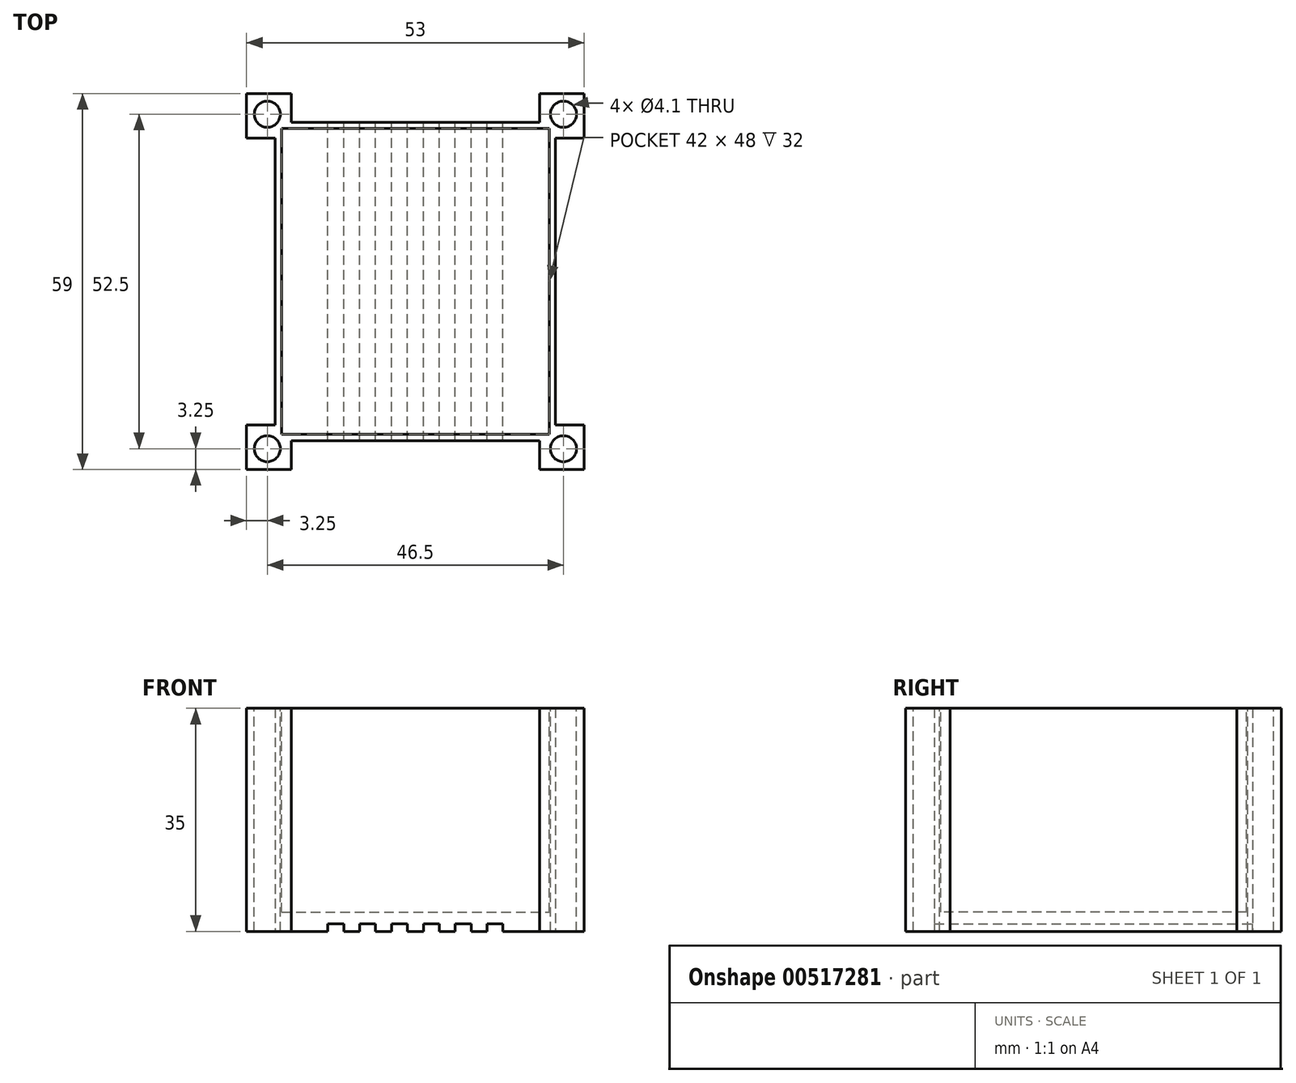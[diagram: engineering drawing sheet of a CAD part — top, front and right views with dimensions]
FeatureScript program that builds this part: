
annotation { "Feature Type Name" : "Feature", "Feature Type Description" : "" }
export const myFeature = defineFeature(function(context is Context, id is Id, definition is map)
    precondition{}
    {
        {
            var Q0;
            Q0=qCreatedBy(makeId("Top.planeOp"),FACE);
            var sketch = newSketch(context, id + "F0", { "sketchPlane" : qUnion([Q0])});
            skLineSegment(sketch, "E0.bottom", {"start": v(-22, 25) * mm, "end": v(22, 25) * mm});
            skLineSegment(sketch, "E0.top", {"start": v(-22, -25) * mm, "end": v(22, -25) * mm});
            skLineSegment(sketch, "E0.left", {"start": v(-22, 25) * mm, "end": v(-22, -25) * mm});
            skLineSegment(sketch, "E0.right", {"start": v(22, 25) * mm, "end": v(22, -25) * mm});
            skLineSegment(sketch, "E1.bottom", {"start": v(-26.5, 29.5) * mm, "end": v(-19.5, 29.5) * mm});
            skLineSegment(sketch, "E1.top", {"start": v(-26.5, 22.5) * mm, "end": v(-19.5, 22.5) * mm});
            skLineSegment(sketch, "E1.left", {"start": v(-26.5, 29.5) * mm, "end": v(-26.5, 22.5) * mm});
            skLineSegment(sketch, "E1.right", {"start": v(-19.5, 29.5) * mm, "end": v(-19.5, 22.5) * mm});
            skLineSegment(sketch, "E2.MirrorCS", {"start": v(19.5, 29.5) * mm, "end": v(19.5, 22.5) * mm});
            skLineSegment(sketch, "E3.MirrorCS", {"start": v(26.5, 22.5) * mm, "end": v(19.5, 22.5) * mm});
            skLineSegment(sketch, "E4.MirrorCS", {"start": v(26.5, 29.5) * mm, "end": v(19.5, 29.5) * mm});
            skLineSegment(sketch, "E5.MirrorCS", {"start": v(26.5, 29.5) * mm, "end": v(26.5, 22.5) * mm});
            skLineSegment(sketch, "E6.MirrorCS", {"start": v(26.5, -29.5) * mm, "end": v(26.5, -22.5) * mm});
            skLineSegment(sketch, "E7.MirrorCS", {"start": v(26.5, -29.5) * mm, "end": v(19.5, -29.5) * mm});
            skLineSegment(sketch, "E8.MirrorCS", {"start": v(26.5, -22.5) * mm, "end": v(19.5, -22.5) * mm});
            skLineSegment(sketch, "E9.MirrorCS", {"start": v(19.5, -29.5) * mm, "end": v(19.5, -22.5) * mm});
            skLineSegment(sketch, "E10.MirrorCS", {"start": v(-19.5, -29.5) * mm, "end": v(-19.5, -22.5) * mm});
            skLineSegment(sketch, "E11.MirrorCS", {"start": v(-26.5, -29.5) * mm, "end": v(-26.5, -22.5) * mm});
            skLineSegment(sketch, "E12.MirrorCS", {"start": v(-26.5, -29.5) * mm, "end": v(-19.5, -29.5) * mm});
            skLineSegment(sketch, "E13.MirrorCS", {"start": v(-26.5, -22.5) * mm, "end": v(-19.5, -22.5) * mm});
            skSolve(sketch);
        }
        {
            var Q0;
            Q0 = qSketchRegion(id + "F0", true);
            extrude(context, id + "F1", {"entities" : qUnion([Q0]), "depth" : 35 * mm, "offsetDistance" : 25 * mm});
        }
        {
            var Q0;
            Q0=makeQuery(id+"F1.opExtrude","CAP_FACE",FACE,{"disambiguationData":[OSD([sQuery(id+"F0.wireOp",EDGE,"E0.bottom"),sQuery(id+"F0.wireOp",EDGE,"E0.top"),sQuery(id+"F0.wireOp",EDGE,"E0.left"),sQuery(id+"F0.wireOp",EDGE,"E0.right"),sQuery(id+"F0.wireOp",EDGE,"E1.bottom"),sQuery(id+"F0.wireOp",EDGE,"E1.top"),sQuery(id+"F0.wireOp",EDGE,"E1.left"),sQuery(id+"F0.wireOp",EDGE,"E1.right"),sQuery(id+"F0.wireOp",EDGE,"E2.MirrorCS"),sQuery(id+"F0.wireOp",EDGE,"E3.MirrorCS"),sQuery(id+"F0.wireOp",EDGE,"E4.MirrorCS"),sQuery(id+"F0.wireOp",EDGE,"E5.MirrorCS"),sQuery(id+"F0.wireOp",EDGE,"E6.MirrorCS"),sQuery(id+"F0.wireOp",EDGE,"E7.MirrorCS"),sQuery(id+"F0.wireOp",EDGE,"E8.MirrorCS"),sQuery(id+"F0.wireOp",EDGE,"E9.MirrorCS"),sQuery(id+"F0.wireOp",EDGE,"E10.MirrorCS"),sQuery(id+"F0.wireOp",EDGE,"E11.MirrorCS"),sQuery(id+"F0.wireOp",EDGE,"E12.MirrorCS"),sQuery(id+"F0.wireOp",EDGE,"E13.MirrorCS")])],"isStart":false});
            var sketch = newSketch(context, id + "F2", { "sketchPlane" : qUnion([Q0])});
            skCircle(sketch, "E14", {"center": v(-23.25, 26.25) * mm, "radius": 2.05 * mm});
            skCircle(sketch, "E15.MirrorC", {"center": v(23.25, 26.25) * mm, "radius": 2.05 * mm});
            skCircle(sketch, "E16.MirrorC", {"center": v(-23.25, -26.25) * mm, "radius": 2.05 * mm});
            skCircle(sketch, "E17.MirrorC", {"center": v(23.25, -26.25) * mm, "radius": 2.05 * mm});
            skSolve(sketch);
        }
        {
            var Q0;
            Q0 = qSketchRegion(id + "F2", true);
            extrude(context, id + "F3", {"entities" : qUnion([Q0]), "operationType" : NewBodyOperationType.REMOVE, "endBound" : BoundingType.UP_TO_NEXT, "oppositeDirection" : true, "depth" : 25 * mm, "offsetDistance" : 25 * mm});
        }
        {
            var Q0;
            Q0=makeQuery(id+"F1.opExtrude","CAP_FACE",FACE,{"disambiguationData":[OSD([sQuery(id+"F0.wireOp",EDGE,"E0.bottom"),sQuery(id+"F0.wireOp",EDGE,"E0.top"),sQuery(id+"F0.wireOp",EDGE,"E0.left"),sQuery(id+"F0.wireOp",EDGE,"E0.right"),sQuery(id+"F0.wireOp",EDGE,"E1.bottom"),sQuery(id+"F0.wireOp",EDGE,"E1.top"),sQuery(id+"F0.wireOp",EDGE,"E1.left"),sQuery(id+"F0.wireOp",EDGE,"E1.right"),sQuery(id+"F0.wireOp",EDGE,"E2.MirrorCS"),sQuery(id+"F0.wireOp",EDGE,"E3.MirrorCS"),sQuery(id+"F0.wireOp",EDGE,"E4.MirrorCS"),sQuery(id+"F0.wireOp",EDGE,"E5.MirrorCS"),sQuery(id+"F0.wireOp",EDGE,"E6.MirrorCS"),sQuery(id+"F0.wireOp",EDGE,"E7.MirrorCS"),sQuery(id+"F0.wireOp",EDGE,"E8.MirrorCS"),sQuery(id+"F0.wireOp",EDGE,"E9.MirrorCS"),sQuery(id+"F0.wireOp",EDGE,"E10.MirrorCS"),sQuery(id+"F0.wireOp",EDGE,"E11.MirrorCS"),sQuery(id+"F0.wireOp",EDGE,"E12.MirrorCS"),sQuery(id+"F0.wireOp",EDGE,"E13.MirrorCS")])],"isStart":false});
            var sketch = newSketch(context, id + "F4", { "sketchPlane" : qUnion([Q0])});
            skLineSegment(sketch, "E18.bottom", {"start": v(-21, 24) * mm, "end": v(21, 24) * mm});
            skLineSegment(sketch, "E18.top", {"start": v(-21, -24) * mm, "end": v(21, -24) * mm});
            skLineSegment(sketch, "E18.left", {"start": v(-21, 24) * mm, "end": v(-21, -24) * mm});
            skLineSegment(sketch, "E18.right", {"start": v(21, 24) * mm, "end": v(21, -24) * mm});
            skSolve(sketch);
        }
        {
            var Q0;
            Q0 = qSketchRegion(id + "F4", true);
            extrude(context, id + "F5", {"entities" : qUnion([Q0]), "operationType" : NewBodyOperationType.REMOVE, "oppositeDirection" : true, "depth" : 32 * mm, "offsetDistance" : 25 * mm});
        }
        {
            var Q0;
            Q0=makeQuery(id+"F1.opExtrude","SWEPT_FACE",FACE,{"disambiguationData":[OSD([sQuery(id+"F0.wireOp",EDGE,"E0.bottom")])]});
            var sketch = newSketch(context, id + "F6", { "sketchPlane" : qUnion([Q0])});
            skLineSegment(sketch, "E19.bottom", {"start": v(13.75, 1.2) * mm, "end": v(11.25, 1.2) * mm});
            skLineSegment(sketch, "E19.top", {"start": v(13.75, 0) * mm, "end": v(11.25, 0) * mm});
            skLineSegment(sketch, "E19.left", {"start": v(13.75, 0) * mm, "end": v(13.75, 1.2) * mm});
            skLineSegment(sketch, "E19.right", {"start": v(11.25, 0) * mm, "end": v(11.25, 1.2) * mm});
            skLineSegment(sketch, "E20.1.0.0", {"start": v(8.75, 1.2) * mm, "end": v(6.25, 1.2) * mm});
            skLineSegment(sketch, "E20.1.0.1", {"start": v(8.75, 0) * mm, "end": v(6.25, 0) * mm});
            skLineSegment(sketch, "E20.1.0.2", {"start": v(8.75, 0) * mm, "end": v(8.75, 1.2) * mm});
            skLineSegment(sketch, "E20.1.0.3", {"start": v(6.25, 0) * mm, "end": v(6.25, 1.2) * mm});
            skLineSegment(sketch, "E20.2.0.0", {"start": v(3.75, 1.2) * mm, "end": v(1.25, 1.2) * mm});
            skLineSegment(sketch, "E20.2.0.1", {"start": v(3.75, 0) * mm, "end": v(1.25, 0) * mm});
            skLineSegment(sketch, "E20.2.0.2", {"start": v(3.75, 0) * mm, "end": v(3.75, 1.2) * mm});
            skLineSegment(sketch, "E20.2.0.3", {"start": v(1.25, 0) * mm, "end": v(1.25, 1.2) * mm});
            skLineSegment(sketch, "E20.3.0.0", {"start": v(-1.25, 1.2) * mm, "end": v(-3.75, 1.2) * mm});
            skLineSegment(sketch, "E20.3.0.1", {"start": v(-1.25, 0) * mm, "end": v(-3.75, 0) * mm});
            skLineSegment(sketch, "E20.3.0.2", {"start": v(-1.25, 0) * mm, "end": v(-1.25, 1.2) * mm});
            skLineSegment(sketch, "E20.3.0.3", {"start": v(-3.75, 0) * mm, "end": v(-3.75, 1.2) * mm});
            skLineSegment(sketch, "E20.4.0.0", {"start": v(-6.25, 1.2) * mm, "end": v(-8.75, 1.2) * mm});
            skLineSegment(sketch, "E20.4.0.1", {"start": v(-6.25, 0) * mm, "end": v(-8.75, 0) * mm});
            skLineSegment(sketch, "E20.4.0.2", {"start": v(-6.25, 0) * mm, "end": v(-6.25, 1.2) * mm});
            skLineSegment(sketch, "E20.4.0.3", {"start": v(-8.75, 0) * mm, "end": v(-8.75, 1.2) * mm});
            skLineSegment(sketch, "E20.5.0.0", {"start": v(-11.25, 1.2) * mm, "end": v(-13.75, 1.2) * mm});
            skLineSegment(sketch, "E20.5.0.1", {"start": v(-11.25, 0) * mm, "end": v(-13.75, 0) * mm});
            skLineSegment(sketch, "E20.5.0.2", {"start": v(-11.25, 0) * mm, "end": v(-11.25, 1.2) * mm});
            skLineSegment(sketch, "E20.5.0.3", {"start": v(-13.75, 0) * mm, "end": v(-13.75, 1.2) * mm});
            skLineSegment(sketch, "E20.direction1", {"start": v(11.25, 1.2) * mm, "end": v(6.25, 1.2) * mm, "construction": true});
            skLineSegment(sketch, "E21", {"start": v(-19.5, 0) * mm, "end": v(-13.75, 0) * mm, "construction": true});
            skLineSegment(sketch, "E22", {"start": v(13.75, 0) * mm, "end": v(19.5, 0) * mm, "construction": true});
            skSolve(sketch);
        }
        {
            var Q0;
            Q0 = qSketchRegion(id + "F6", true);
            var Q1;
            Q1=makeQuery(id+"F1.opExtrude","SWEPT_FACE",FACE,{"disambiguationData":[OSD([sQuery(id+"F0.wireOp",EDGE,"E0.top")])]});
            extrude(context, id + "F7", {"entities" : qUnion([Q0]), "operationType" : NewBodyOperationType.REMOVE, "endBound" : BoundingType.UP_TO_SURFACE, "oppositeDirection" : true, "depth" : 25 * mm, "endBoundEntityFace" : qUnion([Q1]), "offsetDistance" : 25 * mm});
        }
    });
